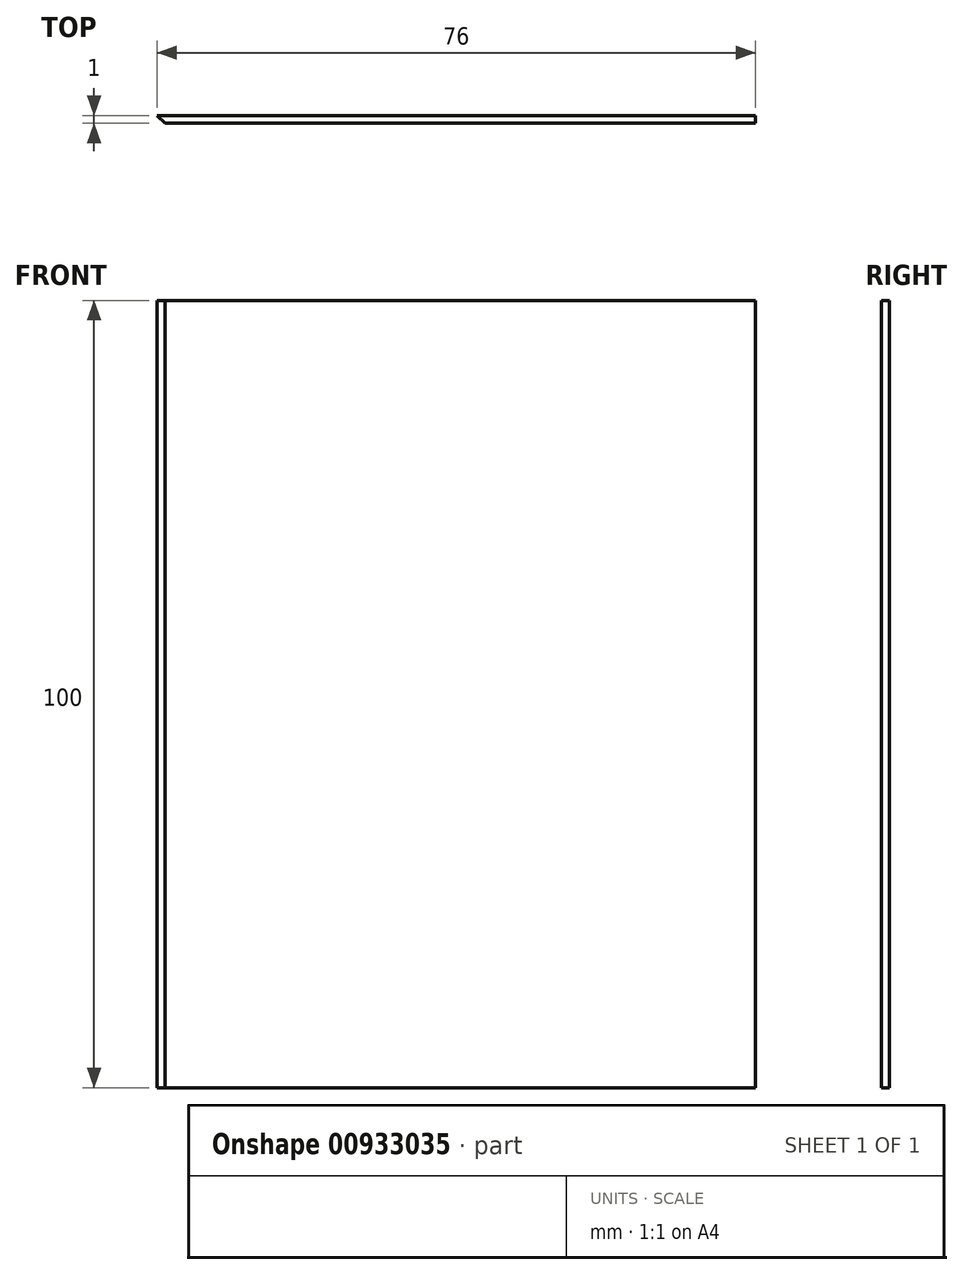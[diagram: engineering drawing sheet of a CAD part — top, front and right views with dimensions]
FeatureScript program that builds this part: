
annotation { "Feature Type Name" : "Feature", "Feature Type Description" : "" }
export const myFeature = defineFeature(function(context is Context, id is Id, definition is map)
    precondition{}
    {
        {
            var Q0;
            Q0=qCreatedBy(makeId("Front.planeOp"),FACE);
            var sketch = newSketch(context, id + "F0", { "sketchPlane" : qUnion([Q0])});
            skLineSegment(sketch, "E0.bottom", {"start": v(-40, 50) * mm, "end": v(40, 50) * mm});
            skLineSegment(sketch, "E0.top", {"start": v(-40, -50) * mm, "end": v(40, -50) * mm});
            skLineSegment(sketch, "E0.left", {"start": v(-40, 50) * mm, "end": v(-40, -50) * mm});
            skLineSegment(sketch, "E0.right", {"start": v(40, 50) * mm, "end": v(40, -50) * mm});
            skSolve(sketch);
        }
        {
            var Q0;
            Q0=makeQuery(id+"F0.imprint","IMPRINT",FACE,{"disambiguationData":[TD([[makeQuery(id+"F0.imprint","IMPRINT",EDGE,{"derivedFrom":sQuery(id+"F0.wireOp",EDGE,"E0.bottom")}),-1.0]])]});
            extrude(context, id + "F1", {"entities" : qUnion([Q0]), "endBound" : BoundingType.SYMMETRIC, "depth" : 1 * mm, "offsetDistance" : 25 * mm});
        }
        {
            var Q0;
            Q0=makeQuery(id+"F1.opExtrude","CAP_EDGE",EDGE,{"disambiguationData":[OSD([sQuery(id+"F0.wireOp",EDGE,"E0.left")])],"isStart":false});
            chamfer(context, id + "F2", {"entities" : qUnion([Q0]), "width" : 5 * mm, "tangentPropagation" : true});
        }
    });
